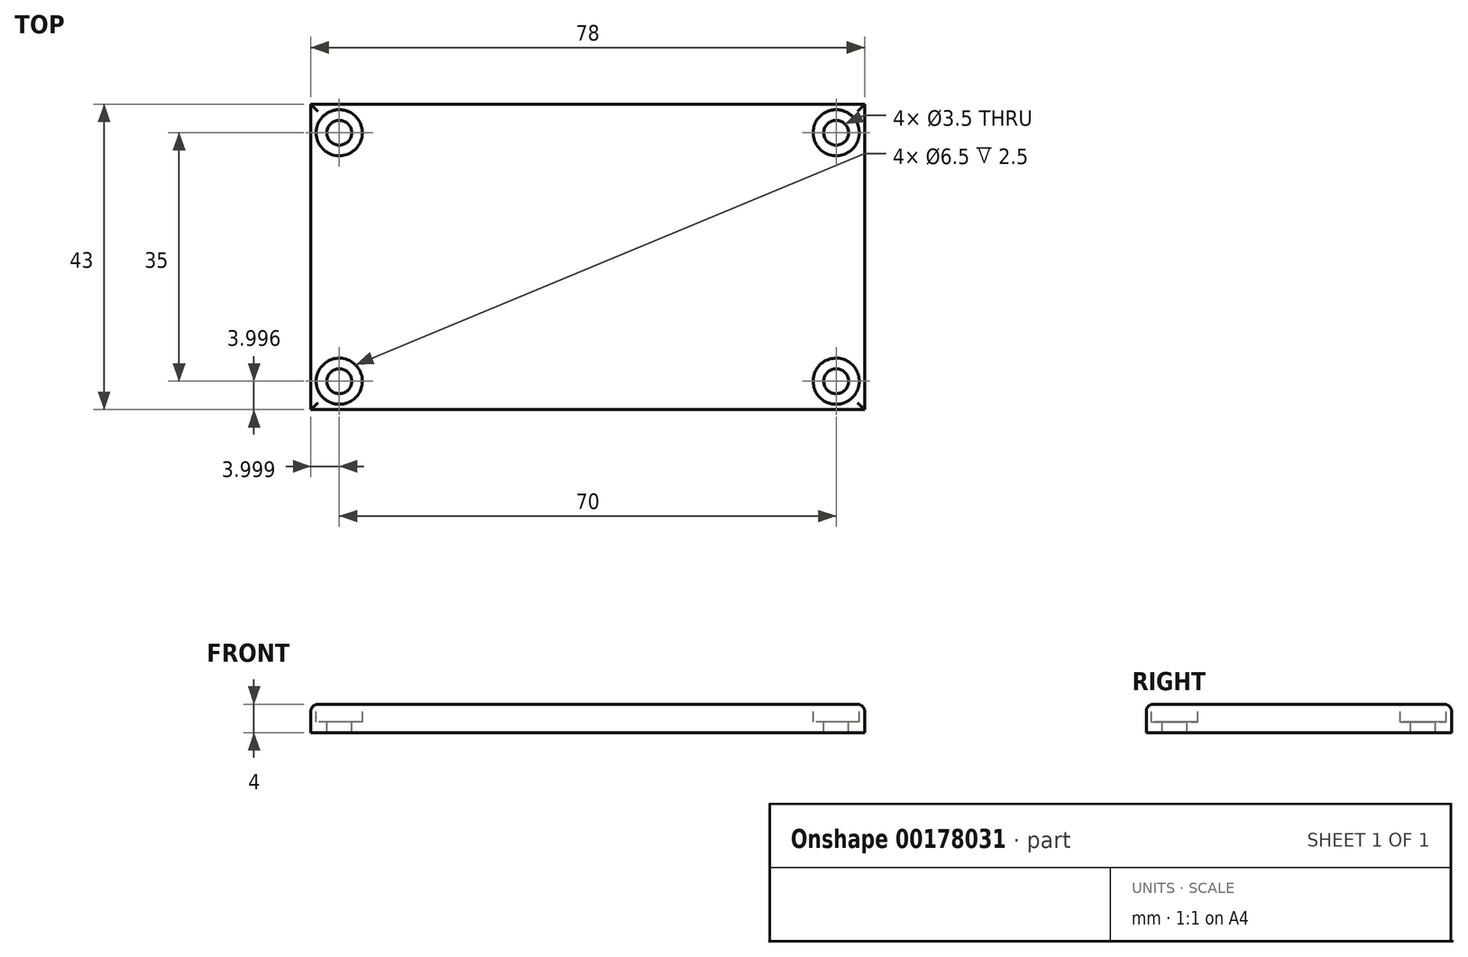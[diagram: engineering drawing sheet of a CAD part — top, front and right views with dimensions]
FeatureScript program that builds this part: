
annotation { "Feature Type Name" : "Feature", "Feature Type Description" : "" }
export const myFeature = defineFeature(function(context is Context, id is Id, definition is map)
    precondition{}
    {
        {
            var Q0;
            Q0=qCreatedBy(makeId("Top.planeOp"),FACE);
            var sketch = newSketch(context, id + "F0", { "sketchPlane" : qUnion([Q0])});
            skLineSegment(sketch, "E0.bottom", {"start": v(-4.04, 3.95) * mm, "end": v(73.96, 3.95) * mm});
            skLineSegment(sketch, "E0.top", {"start": v(-4.04, -39.05) * mm, "end": v(73.96, -39.05) * mm});
            skLineSegment(sketch, "E0.left", {"start": v(-4.04, 3.95) * mm, "end": v(-4.04, -39.05) * mm});
            skLineSegment(sketch, "E0.right", {"start": v(73.96, 3.95) * mm, "end": v(73.96, -39.05) * mm});
            skSolve(sketch);
        }
        {
            var Q0;
            Q0=qSketchRegion(id+"F0",true);
            extrude(context, id + "F1", {"entities" : qUnion([Q0]), "depth" : 4 * mm});
        }
        {
            var Q0;
            Q0=makeQuery(id+"F1.opExtrude","CAP_FACE",FACE,{"disambiguationData":[OSD([sQuery(id+"F0.wireOp",EDGE,"E0.bottom"),sQuery(id+"F0.wireOp",EDGE,"E0.top"),sQuery(id+"F0.wireOp",EDGE,"E0.left"),sQuery(id+"F0.wireOp",EDGE,"E0.right")])],"isStart":false});
            var sketch = newSketch(context, id + "F2", { "sketchPlane" : qUnion([Q0])});
            skLineSegment(sketch, "E1.0", {"start": v(-0.04, -0.05) * mm, "end": v(69.96, -0.05) * mm, "construction": true});
            skLineSegment(sketch, "E1.1", {"start": v(-0.04, -0.05) * mm, "end": v(-0.04, -35.05) * mm, "construction": true});
            skLineSegment(sketch, "E1.2", {"start": v(-0.04, -35.05) * mm, "end": v(69.96, -35.05) * mm, "construction": true});
            skLineSegment(sketch, "E1.3", {"start": v(69.96, -0.05) * mm, "end": v(69.96, -35.05) * mm, "construction": true});
            skCircle(sketch, "E2", {"center": v(-0.04, -0.05) * mm, "radius": 1.75 * mm});
            skCircle(sketch, "E3", {"center": v(69.96, -0.05) * mm, "radius": 1.75 * mm});
            skCircle(sketch, "E4", {"center": v(69.96, -35.05) * mm, "radius": 1.75 * mm});
            skCircle(sketch, "E5", {"center": v(-0.04, -35.05) * mm, "radius": 1.75 * mm});
            skSolve(sketch);
        }
        {
            var Q0;
            Q0=qSketchRegion(id+"F2",true);
            extrude(context, id + "F3", {"entities" : qUnion([Q0]), "operationType" : NewBodyOperationType.REMOVE, "endBound" : BoundingType.THROUGH_ALL, "oppositeDirection" : true, "depth" : 25 * mm});
        }
        {
            var Q0;
            Q0=makeQuery(id+"F1.opExtrude","CAP_FACE",FACE,{"disambiguationData":[OSD([sQuery(id+"F0.wireOp",EDGE,"E0.bottom"),sQuery(id+"F0.wireOp",EDGE,"E0.top"),sQuery(id+"F0.wireOp",EDGE,"E0.left"),sQuery(id+"F0.wireOp",EDGE,"E0.right")])],"isStart":false});
            var sketch = newSketch(context, id + "F4", { "sketchPlane" : qUnion([Q0])});
            skCircle(sketch, "E6", {"center": v(-0.04, -0.05) * mm, "radius": 3.25 * mm});
            skCircle(sketch, "E7", {"center": v(69.96, -0.05) * mm, "radius": 3.25 * mm});
            skCircle(sketch, "E8", {"center": v(69.96, -35.05) * mm, "radius": 3.25 * mm});
            skCircle(sketch, "E9", {"center": v(-0.04, -35.05) * mm, "radius": 3.25 * mm});
            skSolve(sketch);
        }
        {
            var Q0;
            Q0=qSketchRegion(id+"F4",true);
            extrude(context, id + "F5", {"entities" : qUnion([Q0]), "operationType" : NewBodyOperationType.REMOVE, "oppositeDirection" : true, "depth" : 2.5 * mm});
        }
        {
            var Q0;
            Q0=makeQuery(id+"F1.opExtrude","CAP_EDGE",EDGE,{"disambiguationData":[OSD([sQuery(id+"F0.wireOp",EDGE,"E0.left")])],"isStart":false});
            var Q1;
            Q1=makeQuery(id+"F1.opExtrude","CAP_EDGE",EDGE,{"disambiguationData":[OSD([sQuery(id+"F0.wireOp",EDGE,"E0.top")])],"isStart":false});
            var Q2;
            Q2=makeQuery(id+"F1.opExtrude","CAP_EDGE",EDGE,{"disambiguationData":[OSD([sQuery(id+"F0.wireOp",EDGE,"E0.right")])],"isStart":false});
            var Q3;
            Q3=makeQuery(id+"F1.opExtrude","CAP_EDGE",EDGE,{"disambiguationData":[OSD([sQuery(id+"F0.wireOp",EDGE,"E0.bottom")])],"isStart":false});
            fillet(context, id + "F6", {"entities" : qUnion([Q0, Q1, Q2, Q3]), "radius" : 1 * mm, "tangentPropagation" : true, "allowEdgeOverflow" : false});
        }
    });
